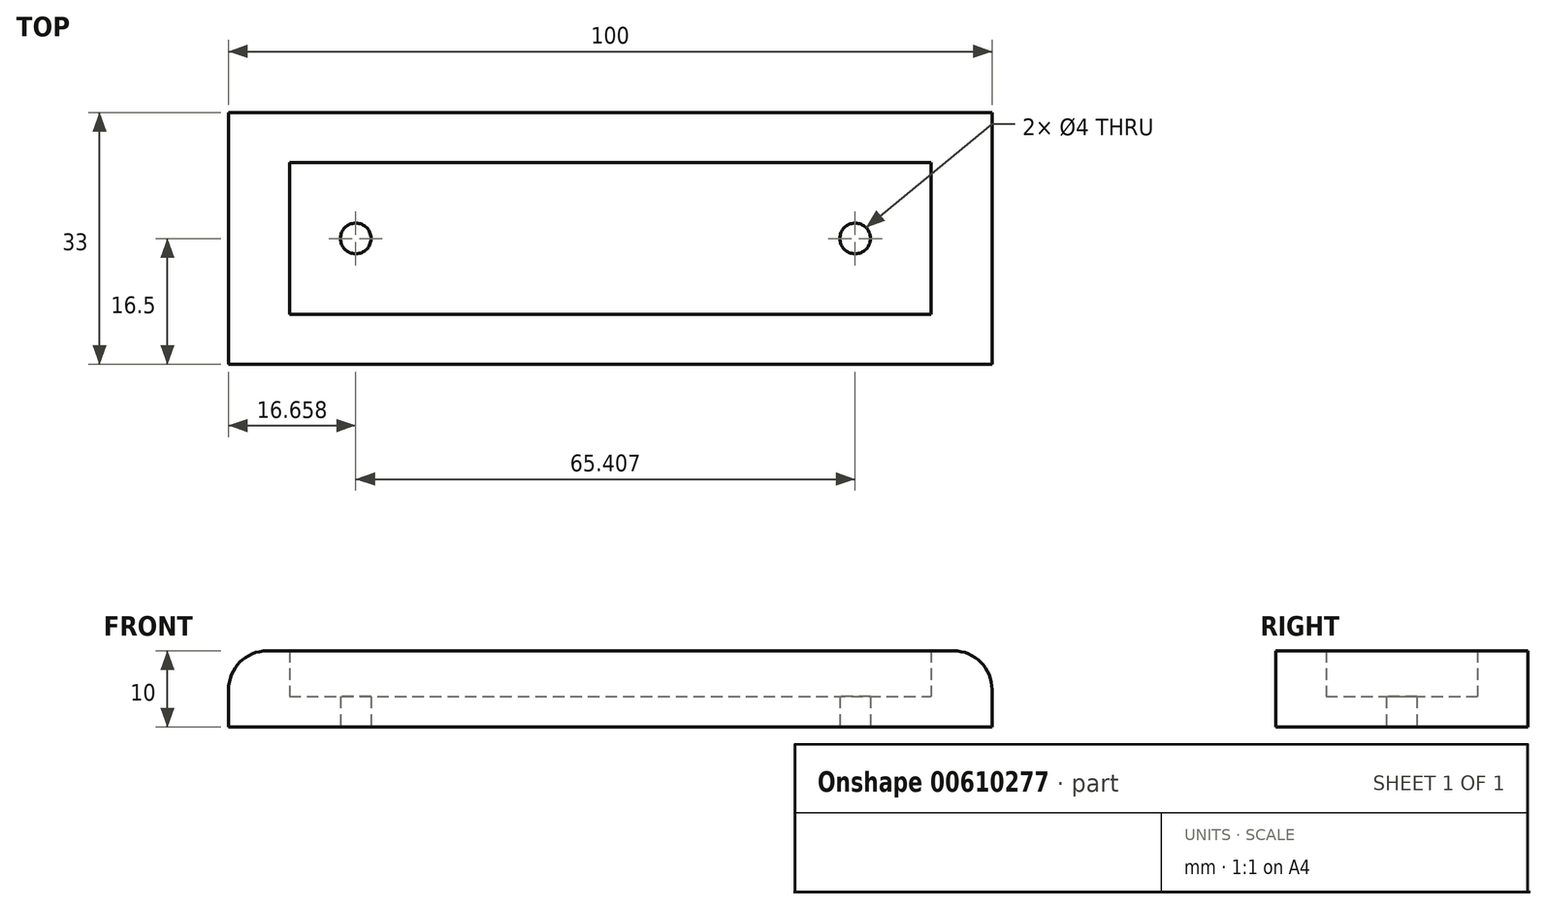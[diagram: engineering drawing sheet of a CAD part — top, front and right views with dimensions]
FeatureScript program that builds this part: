
annotation { "Feature Type Name" : "Feature", "Feature Type Description" : "" }
export const myFeature = defineFeature(function(context is Context, id is Id, definition is map)
    precondition{}
    {
        {
            var Q0;
            Q0=qCreatedBy(makeId("Top.planeOp"),FACE);
            var sketch = newSketch(context, id + "F0", { "sketchPlane" : qUnion([Q0])});
            skLineSegment(sketch, "E0.bottom", {"start": v(50, 16.5) * mm, "end": v(-50, 16.5) * mm});
            skLineSegment(sketch, "E0.top", {"start": v(50, -16.5) * mm, "end": v(-50, -16.5) * mm});
            skLineSegment(sketch, "E0.left", {"start": v(50, 16.5) * mm, "end": v(50, -16.5) * mm});
            skLineSegment(sketch, "E0.right", {"start": v(-50, 16.5) * mm, "end": v(-50, -16.5) * mm});
            skPoint(sketch, "E0.middle", {"position": v(0, 0) * mm});
            skLineSegment(sketch, "E1.bottom", {"start": v(42.03, 9.92) * mm, "end": v(-42.03, 9.92) * mm});
            skLineSegment(sketch, "E1.top", {"start": v(42.03, -9.92) * mm, "end": v(-42.03, -9.92) * mm});
            skLineSegment(sketch, "E1.left", {"start": v(42.03, 9.92) * mm, "end": v(42.03, -9.92) * mm});
            skLineSegment(sketch, "E1.right", {"start": v(-42.03, 9.92) * mm, "end": v(-42.03, -9.92) * mm});
            skCircle(sketch, "E2", {"center": v(-33.34, 0) * mm, "radius": 2 * mm});
            skCircle(sketch, "E3", {"center": v(32.07, 0) * mm, "radius": 2 * mm});
            skSolve(sketch);
        }
        {
            var Q0;
            Q0=makeQuery(id+"F0.imprint","IMPRINT",FACE,{"disambiguationData":[TD([[makeQuery(id+"F0.imprint","IMPRINT",EDGE,{"derivedFrom":sQuery(id+"F0.wireOp",EDGE,"E0.bottom")}),1.0]])]});
            var Q1;
            Q1=makeQuery(id+"F0.imprint","IMPRINT",FACE,{"disambiguationData":[TD([[makeQuery(id+"F0.imprint","IMPRINT",EDGE,{"derivedFrom":sQuery(id+"F0.wireOp",EDGE,"E1.bottom")}),1.0]])]});
            extrude(context, id + "F1", {"entities" : qUnion([Q0, Q1]), "depth" : 4 * mm, "offsetDistance" : 25.4 * mm});
        }
        {
            var Q0;
            Q0 = qSketchRegion(id + "F0", true);
            extrude(context, id + "F2", {"entities" : qUnion([Q0]), "operationType" : NewBodyOperationType.ADD, "depth" : 10 * mm, "offsetDistance" : 25.4 * mm});
        }
        {
            var Q0;
            Q0=makeQuery(id+"F2.opExtrude","CAP_EDGE",EDGE,{"disambiguationData":[OSD([sQuery(id+"F0.wireOp",EDGE,"E0.right")])],"isStart":false});
            var Q1;
            Q1=makeQuery(id+"F2.opExtrude","CAP_EDGE",EDGE,{"disambiguationData":[OSD([sQuery(id+"F0.wireOp",EDGE,"E0.left")])],"isStart":false});
            fillet(context, id + "F3", {"entities" : qUnion([Q0, Q1]), "radius" : 5.08 * mm, "tangentPropagation" : true, "allowEdgeOverflow" : false});
        }
    });
